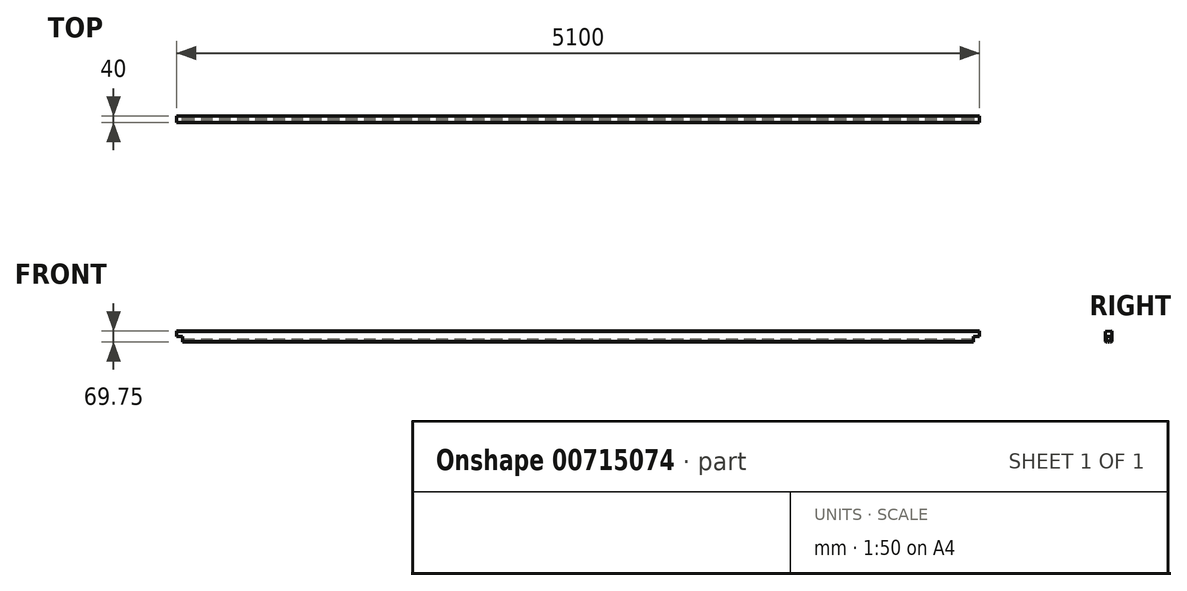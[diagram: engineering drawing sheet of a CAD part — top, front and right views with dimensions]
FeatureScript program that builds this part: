
annotation { "Feature Type Name" : "Feature", "Feature Type Description" : "" }
export const myFeature = defineFeature(function(context is Context, id is Id, definition is map)
    precondition{}
    {
        {
            var Q0;
            Q0=qCreatedBy(makeId("Right.planeOp"),FACE);
            var sketch = newSketch(context, id + "F0", { "sketchPlane" : qUnion([Q0])});
            skLineSegment(sketch, "E0", {"start": v(20, 56) * mm, "end": v(20, -70) * mm});
            skLineSegment(sketch, "E1", {"start": v(20, -70) * mm, "end": v(17, -73) * mm});
            skLineSegment(sketch, "E2", {"start": v(17, -73) * mm, "end": v(12, -73) * mm});
            skLineSegment(sketch, "E3", {"start": v(12, -59) * mm, "end": v(12, -73) * mm});
            skLineSegment(sketch, "E4", {"start": v(12, -59) * mm, "end": v(4, -59) * mm});
            skLineSegment(sketch, "E5", {"start": v(4, -73) * mm, "end": v(4, -59) * mm});
            skLineSegment(sketch, "E6", {"start": v(4, -73) * mm, "end": v(-4, -73) * mm});
            skLineSegment(sketch, "E7", {"start": v(-4, -59) * mm, "end": v(-4, -73) * mm});
            skLineSegment(sketch, "E8", {"start": v(-4, -59) * mm, "end": v(-12, -59) * mm});
            skLineSegment(sketch, "E9", {"start": v(-12, -73) * mm, "end": v(-12, -59) * mm});
            skLineSegment(sketch, "E10", {"start": v(-12, -73) * mm, "end": v(-17, -73) * mm});
            skLineSegment(sketch, "E11", {"start": v(-17, -73) * mm, "end": v(-20, -70) * mm});
            skLineSegment(sketch, "E12", {"start": v(-20, -70) * mm, "end": v(-20, 56) * mm});
            skLineSegment(sketch, "E13", {"start": v(-20, 56) * mm, "end": v(-17, 59) * mm});
            skLineSegment(sketch, "E14", {"start": v(-17, 59) * mm, "end": v(-12, 59) * mm});
            skLineSegment(sketch, "E15", {"start": v(-4, 59) * mm, "end": v(4, 59) * mm});
            skLineSegment(sketch, "E16", {"start": v(12, 59) * mm, "end": v(17, 59) * mm});
            skLineSegment(sketch, "E17", {"start": v(17, 59) * mm, "end": v(20, 56) * mm});
            skPoint(sketch, "E18.end.orphan", {"position": v(12, 57.8) * mm});
            skPoint(sketch, "E19.end.orphan", {"position": v(4, 66.3) * mm});
            skPoint(sketch, "E20.end.orphan", {"position": v(-4, 66.3) * mm});
            skLineSegment(sketch, "E21", {"start": v(-12, 59) * mm, "end": v(-12, 73) * mm});
            skLineSegment(sketch, "E22", {"start": v(-12, 73) * mm, "end": v(-4, 73) * mm});
            skLineSegment(sketch, "E23", {"start": v(-4, 73) * mm, "end": v(-4, 59) * mm});
            skLineSegment(sketch, "E24", {"start": v(4, 59) * mm, "end": v(4, 73) * mm});
            skLineSegment(sketch, "E25", {"start": v(4, 73) * mm, "end": v(12, 73) * mm});
            skLineSegment(sketch, "E26", {"start": v(12, 73) * mm, "end": v(12, 59) * mm});
            skSolve(sketch);
        }
        {
            var Q0;
            Q0=makeQuery(id+"F0.imprint","IMPRINT",FACE,{"disambiguationData":[TD([[makeQuery(id+"F0.imprint","IMPRINT",EDGE,{"derivedFrom":sQuery(id+"F0.wireOp",EDGE,"E0")}),-1.0]])]});
            extrude(context, id + "F1", {"entities" : qUnion([Q0]), "endBound" : BoundingType.SYMMETRIC, "depth" : 5100 * mm, "offsetDistance" : 25 * mm});
        }
        {
            var Q0;
            Q0=qCreatedBy(makeId("Front.planeOp"),FACE);
            var sketch = newSketch(context, id + "F2", { "sketchPlane" : qUnion([Q0])});
            skLineSegment(sketch, "E27.bottom", {"start": v(-2510, 92) * mm, "end": v(-2590, 92) * mm});
            skLineSegment(sketch, "E27.top", {"start": v(-2510, 26) * mm, "end": v(-2590, 26) * mm});
            skLineSegment(sketch, "E27.left", {"start": v(-2510, 92) * mm, "end": v(-2510, 26) * mm});
            skLineSegment(sketch, "E27.right", {"start": v(-2590, 92) * mm, "end": v(-2590, 26) * mm});
            skPoint(sketch, "E27.middle", {"position": v(-2550, 59) * mm});
            skLineSegment(sketch, "E28.bottom", {"start": v(-2510, -40) * mm, "end": v(-2590, -40) * mm});
            skLineSegment(sketch, "E28.top", {"start": v(-2510, -106) * mm, "end": v(-2590, -106) * mm});
            skLineSegment(sketch, "E28.left", {"start": v(-2510, -40) * mm, "end": v(-2510, -106) * mm});
            skLineSegment(sketch, "E28.right", {"start": v(-2590, -40) * mm, "end": v(-2590, -106) * mm});
            skPoint(sketch, "E28.middle", {"position": v(-2550, -73) * mm});
            skLineSegment(sketch, "E29.bottom", {"start": v(2510, 92) * mm, "end": v(2590, 92) * mm});
            skLineSegment(sketch, "E29.top", {"start": v(2510, 26) * mm, "end": v(2590, 26) * mm});
            skLineSegment(sketch, "E29.left", {"start": v(2510, 92) * mm, "end": v(2510, 26) * mm});
            skLineSegment(sketch, "E29.right", {"start": v(2590, 92) * mm, "end": v(2590, 26) * mm});
            skPoint(sketch, "E29.middle", {"position": v(2550, 59) * mm});
            skLineSegment(sketch, "E30.bottom", {"start": v(2510, -106) * mm, "end": v(2590, -106) * mm});
            skLineSegment(sketch, "E30.top", {"start": v(2510, -40) * mm, "end": v(2590, -40) * mm});
            skLineSegment(sketch, "E30.left", {"start": v(2510, -106) * mm, "end": v(2510, -40) * mm});
            skLineSegment(sketch, "E30.right", {"start": v(2590, -106) * mm, "end": v(2590, -40) * mm});
            skPoint(sketch, "E30.middle", {"position": v(2550, -73) * mm});
            skSolve(sketch);
        }
        {
            var Q0;
            Q0=makeQuery(id+"F2.imprint","IMPRINT",FACE,{"disambiguationData":[TD([[makeQuery(id+"F2.imprint","IMPRINT",EDGE,{"derivedFrom":sQuery(id+"F2.wireOp",EDGE,"E27.bottom")}),1.0]])]});
            var Q1;
            Q1=makeQuery(id+"F2.imprint","IMPRINT",FACE,{"disambiguationData":[TD([[makeQuery(id+"F2.imprint","IMPRINT",EDGE,{"derivedFrom":sQuery(id+"F2.wireOp",EDGE,"E28.bottom")}),1.0]])]});
            var Q2;
            Q2=makeQuery(id+"F2.imprint","IMPRINT",FACE,{"disambiguationData":[TD([[makeQuery(id+"F2.imprint","IMPRINT",EDGE,{"derivedFrom":sQuery(id+"F2.wireOp",EDGE,"E29.bottom")}),-1.0]])]});
            var Q3;
            Q3=makeQuery(id+"F2.imprint","IMPRINT",FACE,{"disambiguationData":[TD([[makeQuery(id+"F2.imprint","IMPRINT",EDGE,{"derivedFrom":sQuery(id+"F2.wireOp",EDGE,"E30.bottom")}),1.0]])]});
            extrude(context, id + "F3", {"entities" : qUnion([Q0, Q1, Q2, Q3]), "operationType" : NewBodyOperationType.REMOVE, "endBound" : BoundingType.SYMMETRIC, "oppositeDirection" : true, "depth" : 100 * mm, "offsetDistance" : 25 * mm});
        }
        {
            var Q0;
            Q0=qCreatedBy(makeId("Right.planeOp"),FACE);
            var sketch = newSketch(context, id + "F4", { "sketchPlane" : qUnion([Q0])});
            skLineSegment(sketch, "E31.bottom", {"start": v(-20, -40) * mm, "end": v(20, -40) * mm});
            skLineSegment(sketch, "E31.top", {"start": v(-20, -73) * mm, "end": v(20, -73) * mm});
            skLineSegment(sketch, "E31.left", {"start": v(-20, -40) * mm, "end": v(-20, -73) * mm});
            skLineSegment(sketch, "E31.right", {"start": v(20, -40) * mm, "end": v(20, -73) * mm});
            skSolve(sketch);
        }
        {
            var Q0;
            Q0=qCreatedBy(makeId("Right.planeOp"),FACE);
            var sketch = newSketch(context, id + "F5", { "sketchPlane" : qUnion([Q0])});
            skLineSegment(sketch, "E32", {"start": v(30, 83) * mm, "end": v(-30, 83) * mm});
            skLineSegment(sketch, "E33", {"start": v(-30, 83) * mm, "end": v(-30, -7.94) * mm});
            skLineSegment(sketch, "E34", {"start": v(-30, -7.94) * mm, "end": v(30, -2.32) * mm});
            skLineSegment(sketch, "E35", {"start": v(30, -2.32) * mm, "end": v(30, 83) * mm});
            skSolve(sketch);
        }
        {
            var Q0;
            Q0=makeQuery(id+"F5.imprint","IMPRINT",FACE,{"disambiguationData":[TD([[makeQuery(id+"F5.imprint","IMPRINT",EDGE,{"derivedFrom":sQuery(id+"F5.wireOp",EDGE,"E32")}),1.0]])]});
            extrude(context, id + "F6", {"entities" : qUnion([Q0]), "operationType" : NewBodyOperationType.REMOVE, "endBound" : BoundingType.THROUGH_ALL, "oppositeDirection" : true, "depth" : 25 * mm, "offsetDistance" : 25 * mm, "hasSecondDirection" : true, "secondDirectionBound" : SecondDirectionBoundingType.THROUGH_ALL, "secondDirectionOppositeDirection" : false, "secondDirectionDepth" : 25 * mm});
        }
    });
